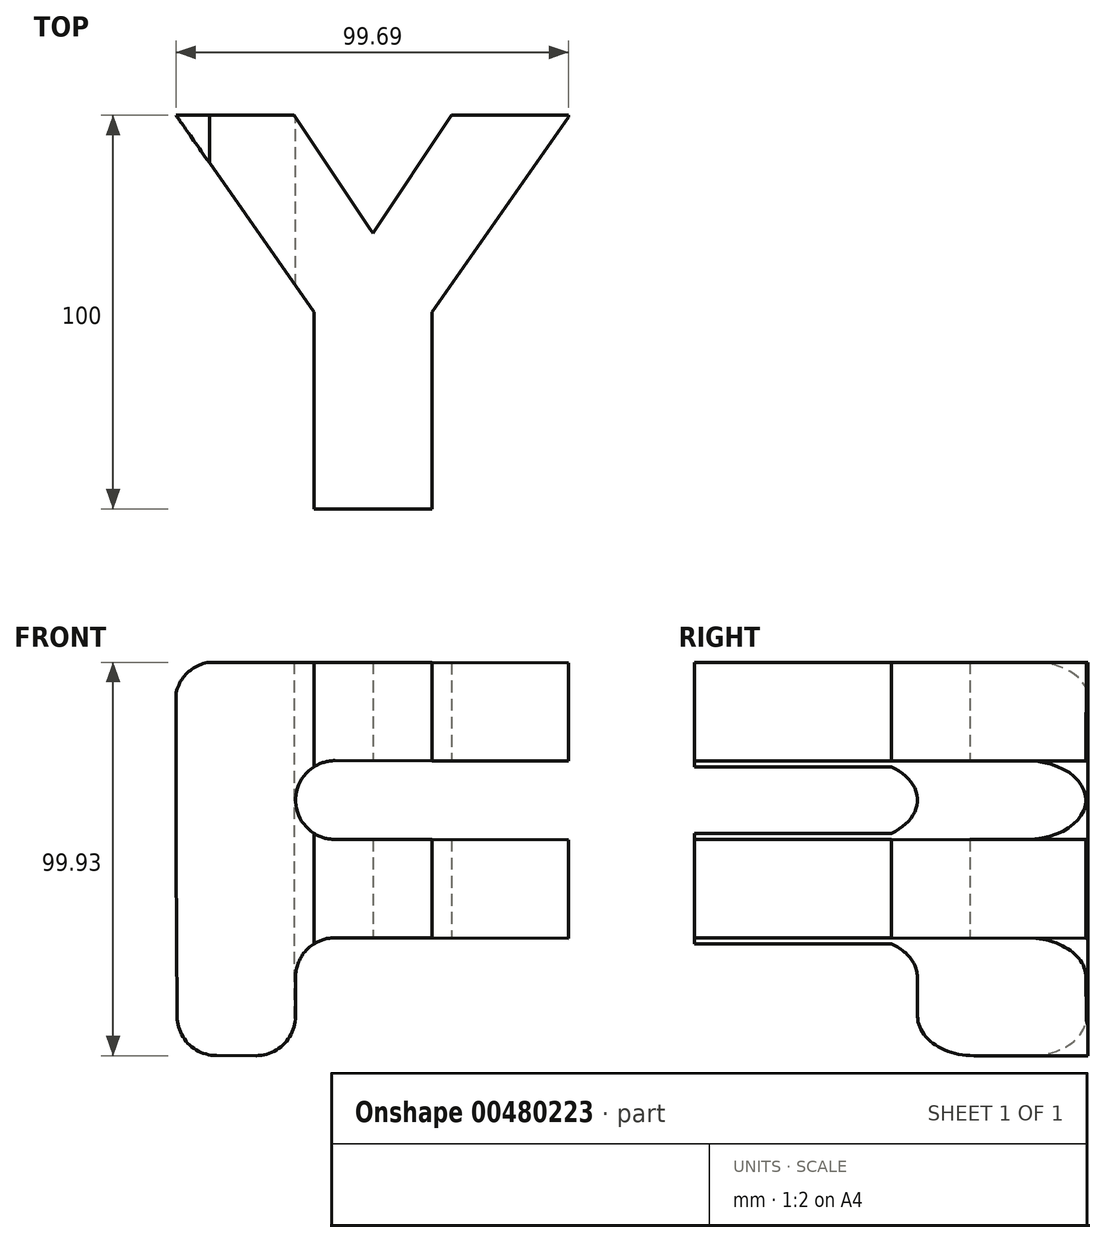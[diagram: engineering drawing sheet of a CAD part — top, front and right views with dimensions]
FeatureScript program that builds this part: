
annotation { "Feature Type Name" : "Feature", "Feature Type Description" : "" }
export const myFeature = defineFeature(function(context is Context, id is Id, definition is map)
    precondition{}
    {
        {
            var Q0;
            Q0=qCreatedBy(makeId("Top.planeOp"),FACE);
            var sketch = newSketch(context, id + "F0", { "sketchPlane" : qUnion([Q0])});
            skLineSegment(sketch, "E0.bottom", {"start": v(50, 50) * mm, "end": v(20, 50) * mm, "construction": true});
            skLineSegment(sketch, "E0.top", {"start": v(15, -50) * mm, "end": v(-15, -50) * mm, "construction": true});
            skPoint(sketch, "E0.middle", {"position": v(0, 0) * mm});
            skLineSegment(sketch, "E1", {"start": v(-50, 50) * mm, "end": v(-20, 50) * mm});
            skLineSegment(sketch, "E2", {"start": v(50, 50) * mm, "end": v(20, 50) * mm});
            skLineSegment(sketch, "E3", {"start": v(-20, 50) * mm, "end": v(0, 20) * mm});
            skLineSegment(sketch, "E4", {"start": v(0, 20) * mm, "end": v(20, 50) * mm});
            skLineSegment(sketch, "E5", {"start": v(-50, 50) * mm, "end": v(-15, 0) * mm});
            skLineSegment(sketch, "E6", {"start": v(50, 50) * mm, "end": v(15, 0) * mm});
            skLineSegment(sketch, "E7.top", {"start": v(-15, -50) * mm, "end": v(15, -50) * mm});
            skLineSegment(sketch, "E7.left", {"start": v(-15, 0) * mm, "end": v(-15, -50) * mm});
            skLineSegment(sketch, "E7.right", {"start": v(15, 0) * mm, "end": v(15, -50) * mm});
            skLineSegment(sketch, "E8.trimOffspring", {"start": v(-20, 50) * mm, "end": v(-50, 50) * mm, "construction": true});
            skPoint(sketch, "E9.orphan", {"position": v(-50, -50) * mm});
            skPoint(sketch, "E0.left.end.orphan", {"position": v(50, -50) * mm});
            skSolve(sketch);
        }
        {
            var Q0;
            Q0=qCreatedBy(makeId("Front.planeOp"),FACE);
            var sketch = newSketch(context, id + "F1", { "sketchPlane" : qUnion([Q0])});
            skLineSegment(sketch, "E10.bottom", {"start": v(49.7, 49.89) * mm, "end": v(-50.3, 50.1) * mm, "construction": true});
            skLineSegment(sketch, "E10.right", {"start": v(-50.3, 50.1) * mm, "end": v(-49.7, -49.89) * mm, "construction": true});
            skPoint(sketch, "E10.middle", {"position": v(0, 0) * mm});
            skLineSegment(sketch, "E11", {"start": v(-50.24, 40.02) * mm, "end": v(-49.75, -39.97) * mm});
            skLineSegment(sketch, "E12", {"start": v(-40.22, 50.09) * mm, "end": v(49.7, 49.89) * mm});
            skLineSegment(sketch, "E13", {"start": v(49.7, 49.89) * mm, "end": v(49.64, 24.9) * mm});
            skLineSegment(sketch, "E14", {"start": v(49.64, 24.9) * mm, "end": v(-9.63, 25.02) * mm});
            skLineSegment(sketch, "E15", {"start": v(-19.65, 15.04) * mm, "end": v(-19.65, 15.04) * mm});
            skLineSegment(sketch, "E16", {"start": v(-9.67, 5.02) * mm, "end": v(49.64, 4.9) * mm});
            skLineSegment(sketch, "E17", {"start": v(49.64, 4.9) * mm, "end": v(49.64, -20.1) * mm});
            skLineSegment(sketch, "E18", {"start": v(49.64, -20.1) * mm, "end": v(-9.63, -19.98) * mm});
            skLineSegment(sketch, "E19", {"start": v(-19.65, -29.96) * mm, "end": v(-19.67, -39.96) * mm});
            skLineSegment(sketch, "E20", {"start": v(-29.7, -49.93) * mm, "end": v(-39.78, -49.91) * mm});
            skPoint(sketch, "E21.visualSharp", {"position": v(-19.63, 25.04) * mm});
            skArc(sketch, "E21.filletArc", {"start": v(-9.63, 25.02) * mm, "mid": v(-16.7, 22.1) * mm, "end": v(-19.65, 15.04) * mm});
            skPoint(sketch, "E22.visualSharp", {"position": v(-19.67, 5.04) * mm});
            skArc(sketch, "E22.filletArc", {"start": v(-19.65, 15.04) * mm, "mid": v(-16.74, 7.96) * mm, "end": v(-9.67, 5.02) * mm});
            skPoint(sketch, "E23.visualSharp", {"position": v(-19.63, -19.96) * mm});
            skArc(sketch, "E23.filletArc", {"start": v(-9.63, -19.98) * mm, "mid": v(-16.7, -22.9) * mm, "end": v(-19.65, -29.96) * mm});
            skPoint(sketch, "E24.visualSharp", {"position": v(-19.7, -49.96) * mm});
            skArc(sketch, "E24.filletArc", {"start": v(-29.7, -49.93) * mm, "mid": v(-22.62, -47.02) * mm, "end": v(-19.67, -39.96) * mm});
            skPoint(sketch, "E25.visualSharp", {"position": v(-49.7, -49.89) * mm});
            skArc(sketch, "E25.filletArc", {"start": v(-49.75, -39.97) * mm, "mid": v(-46.81, -47) * mm, "end": v(-39.78, -49.91) * mm});
            skPoint(sketch, "E26.visualSharp", {"position": v(-50.3, 50.1) * mm});
            skArc(sketch, "E26.filletArc", {"start": v(-40.22, 50.09) * mm, "mid": v(-47.33, 47.14) * mm, "end": v(-50.24, 40.02) * mm});
            skSolve(sketch);
        }
        {
            var Q0;
            Q0=qSketchRegion(id+"F0",true);
            extrude(context, id + "F2", {"entities" : qUnion([Q0]), "endBound" : BoundingType.SYMMETRIC, "depth" : 100 * mm});
        }
        {
            var Q0;
            Q0=qSketchRegion(id+"F1",true);
            extrude(context, id + "F3", {"entities" : qUnion([Q0]), "operationType" : NewBodyOperationType.INTERSECT, "endBound" : BoundingType.SYMMETRIC, "depth" : 100 * mm});
        }
    });
